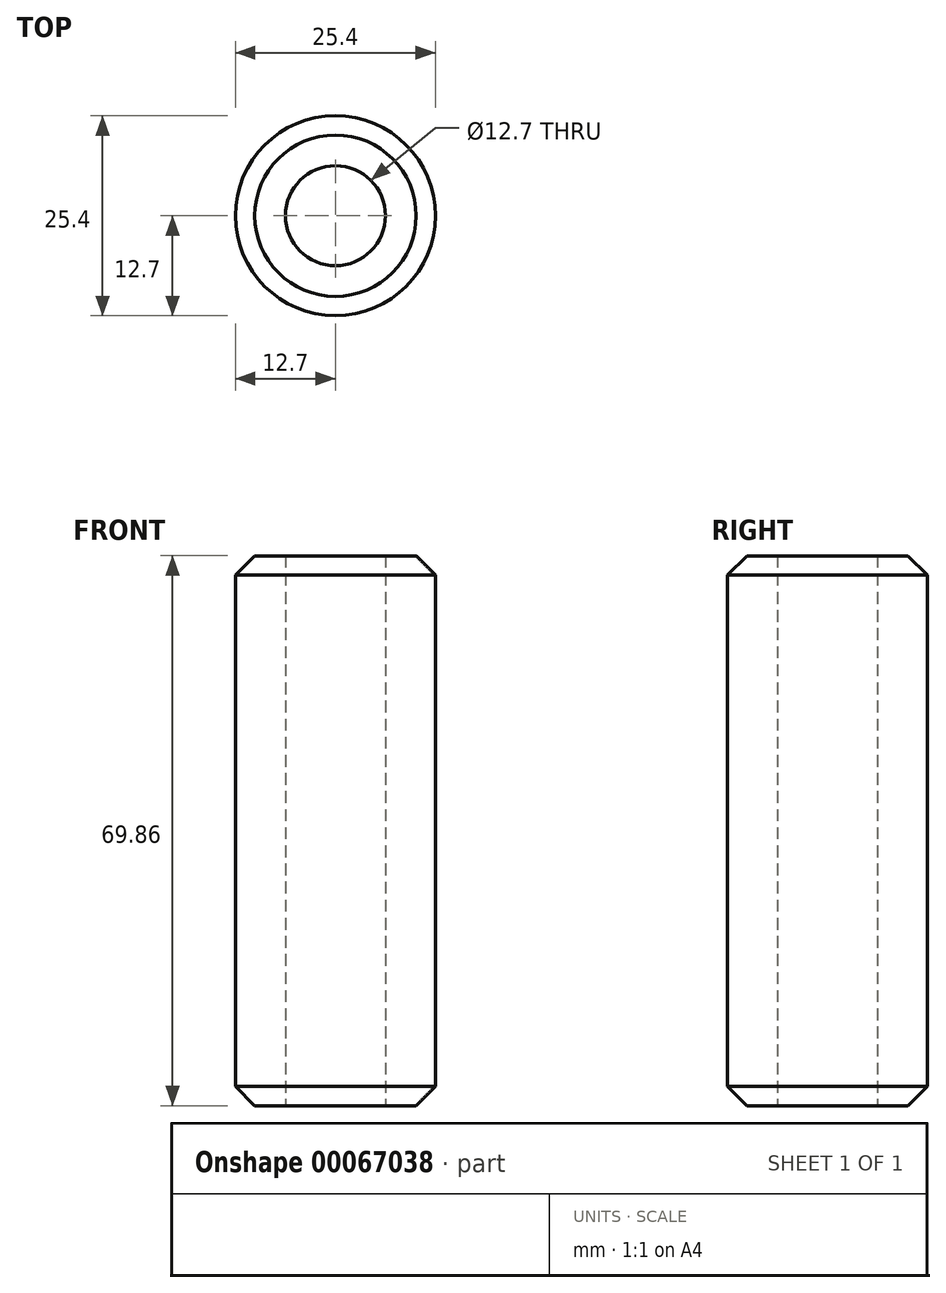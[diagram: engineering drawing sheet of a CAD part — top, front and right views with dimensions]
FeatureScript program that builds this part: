
annotation { "Feature Type Name" : "Feature", "Feature Type Description" : "" }
export const myFeature = defineFeature(function(context is Context, id is Id, definition is map)
    precondition{}
    {
        {
            var Q0;
            Q0=qCreatedBy(makeId("Top.planeOp"),FACE);
            var sketch = newSketch(context, id + "F0", { "sketchPlane" : qUnion([Q0])});
            skCircle(sketch, "E0", {"center": v(0, 0) * mm, "radius": 12.7 * mm});
            skCircle(sketch, "E1", {"center": v(0, 0) * mm, "radius": 6.35 * mm});
            skSolve(sketch);
        }
        {
            var Q0;
            Q0=qSketchRegion(id+"F0",true);
            extrude(context, id + "F1", {"entities" : qUnion([Q0]), "endBound" : BoundingType.SYMMETRIC, "depth" : 69.85 * mm});
        }
        {
            var Q0;
            Q0=makeQuery(id+"F1.opExtrude","CAP_EDGE",EDGE,{"disambiguationData":[OSD([sQuery(id+"F0.wireOp",EDGE,"E0")])],"isStart":true});
            var Q1;
            Q1=makeQuery(id+"F1.opExtrude","CAP_EDGE",EDGE,{"disambiguationData":[OSD([sQuery(id+"F0.wireOp",EDGE,"E0")])],"isStart":false});
            chamfer(context, id + "F2", {"entities" : qUnion([Q0, Q1]), "width" : 2.45 * mm, "tangentPropagation" : true});
        }
    });
